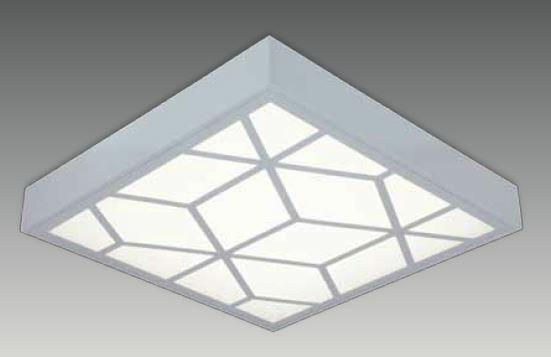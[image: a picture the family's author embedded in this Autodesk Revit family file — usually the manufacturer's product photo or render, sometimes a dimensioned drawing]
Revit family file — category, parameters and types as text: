
# Revit family: S 6060 CUB
name_source: partatom
category: Lighting Fixtures
revit_build: Autodesk Revit 2017 (Build: 20160225_1515(x64)
units: mm (PartAtom-declared; Revit-internal decimal feet)

## family parameters
Always vertical = Yes
Cut with Voids When Loaded = No
Host = Ceiling
Light Source = Yes
OmniClass Number = 23.80.70.11
OmniClass Title = Luminaries for Internal Lighting
Part Type = Normal
Room Calculation Point = No
Round Connector Dimension = Use Diameter
Shared = No

## types (4) — shared parameters
Color Filter = 16777215
Dimming Lamp Color Temperature Shift = <None>
Emit Shape Visible in Rendering = Yes
Emit from Rectangle Length = 570 mm  [stored 1.87008 ft]
Emit from Rectangle Width = 570 mm  [stored 1.87008 ft]
Light Source Symbol Size = 610 mm
Manufacturer = ARLIGHT
Type Image = SD 6060 CUB.JPG

## per-type parameters (varying)
| type | Wattage Comments |
| SDCUB.6060.36.30 | 36 |
| SDCUB.6060.36.40 | 36 |
| SDCUB.6060.28.30 | 28 |
| SDCUB.6060.28.40 | 28 |

note: [stored X ft] marks values corroborated as IEEE doubles in the binary element streams (Revit-internal decimal feet)

## geometry (parser evidence)
native form markers: Sweep x2
no freeform markers — native parametric forms only
